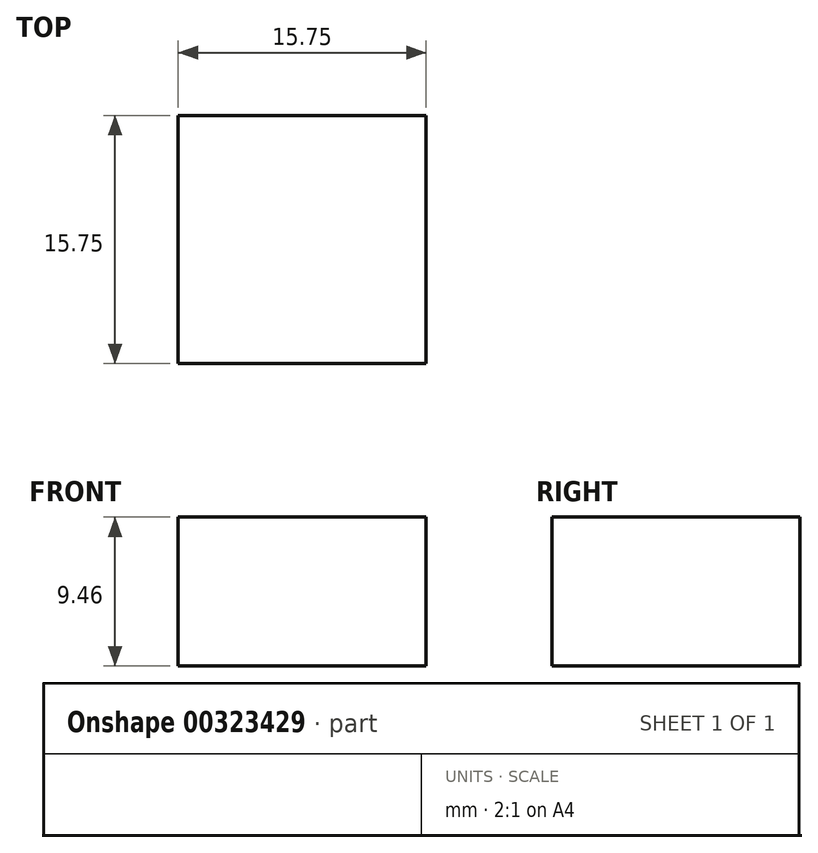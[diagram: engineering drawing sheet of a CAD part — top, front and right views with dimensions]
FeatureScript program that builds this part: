
annotation { "Feature Type Name" : "Feature", "Feature Type Description" : "" }
export const myFeature = defineFeature(function(context is Context, id is Id, definition is map)
    precondition{}
    {
        {
            var Q0;
            Q0=qCreatedBy(makeId("Top.planeOp"),FACE);
            var sketch = newSketch(context, id + "F0", { "sketchPlane" : qUnion([Q0])});
            skLineSegment(sketch, "E0.bottom", {"start": v(0, 0) * mm, "end": v(15.75, 0) * mm});
            skLineSegment(sketch, "E0.top", {"start": v(0, 15.75) * mm, "end": v(15.75, 15.75) * mm});
            skLineSegment(sketch, "E0.left", {"start": v(0, 0) * mm, "end": v(0, 15.75) * mm});
            skLineSegment(sketch, "E0.right", {"start": v(15.75, 0) * mm, "end": v(15.75, 15.75) * mm});
            skSolve(sketch);
        }
        {
            var Q0;
            Q0=makeQuery(id+"F0.imprint","IMPRINT",FACE,{"disambiguationData":[TD([[makeQuery(id+"F0.imprint","IMPRINT",EDGE,{"derivedFrom":sQuery(id+"F0.wireOp",EDGE,"E0.bottom")}),1.0]])]});
            extrude(context, id + "F1", {"entities" : qUnion([Q0]), "depth" : 9.46 * mm});
        }
    });
